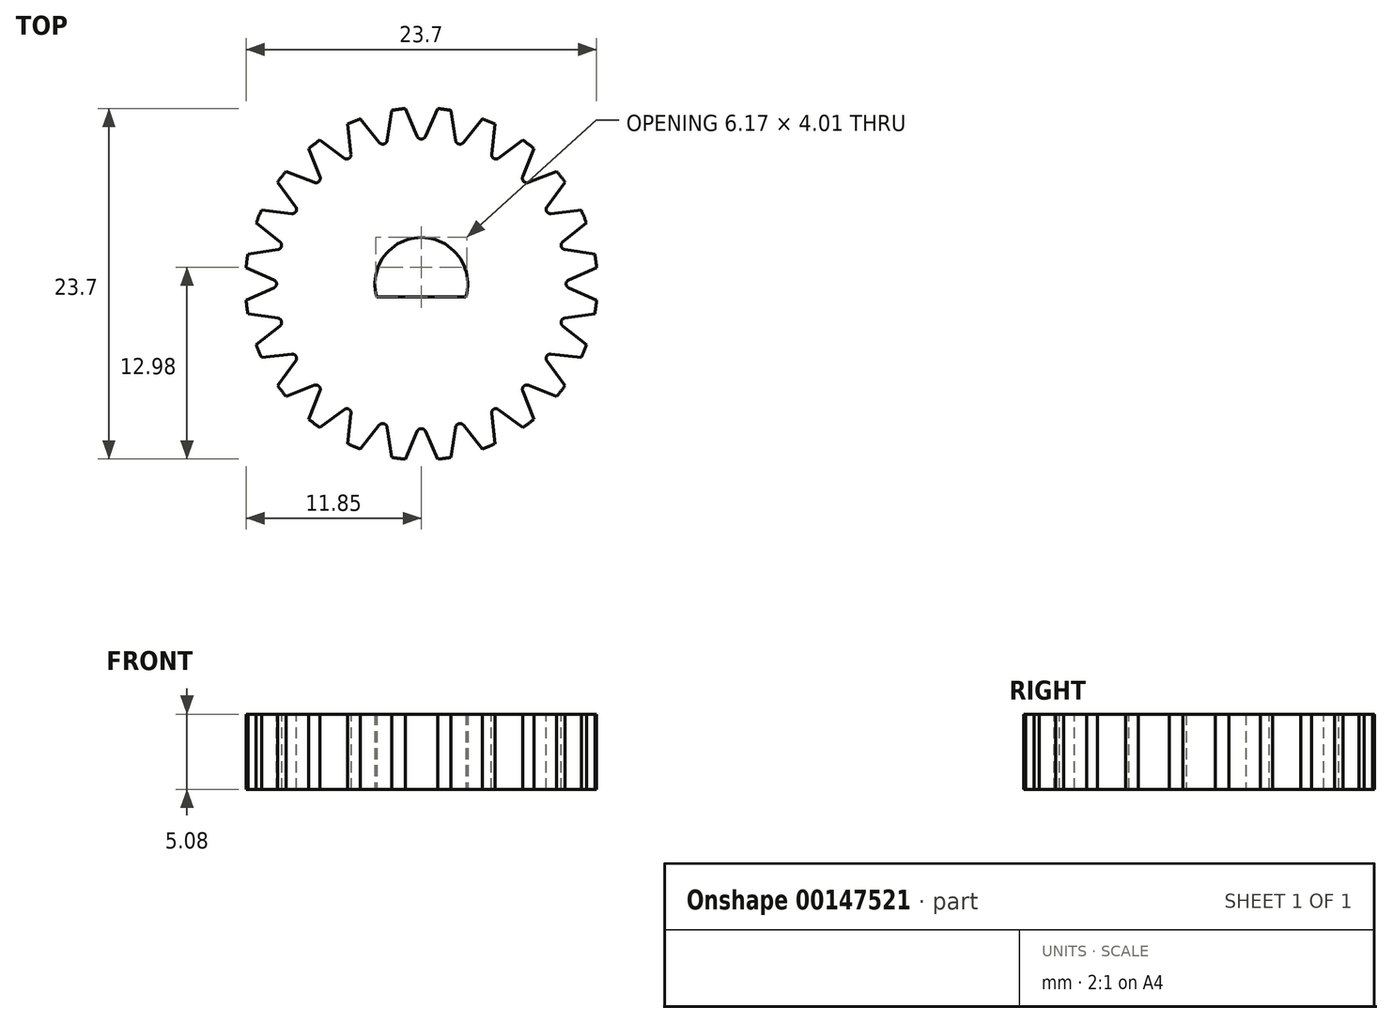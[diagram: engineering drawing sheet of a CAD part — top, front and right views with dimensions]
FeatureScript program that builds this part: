
annotation { "Feature Type Name" : "Feature", "Feature Type Description" : "" }
export const myFeature = defineFeature(function(context is Context, id is Id, definition is map)
    precondition{}
    {
        {
            var Q0;
            Q0=qCreatedBy(makeId("Top.planeOp"),FACE);
            var sketch = newSketch(context, id + "F0", { "sketchPlane" : qUnion([Q0])});
            skCircle(sketch, "E0", {"center": v(0, 0) * mm, "radius": 11.9 * mm});
            skArc(sketch, "E1", {"start": v(3.01, -0.88) * mm, "mid": v(0, 3.14) * mm, "end": v(-3.01, -0.88) * mm});
            skLineSegment(sketch, "E2", {"start": v(0, 0) * mm, "end": v(0, -0.88) * mm, "construction": true});
            skLineSegment(sketch, "E3", {"start": v(-3.01, -0.88) * mm, "end": v(3.01, -0.88) * mm});
            skSolve(sketch);
        }
        {
            var Q0;
            Q0=qSketchRegion(id+"F0",true);
            extrude(context, id + "F1", {"entities" : qUnion([Q0]), "depth" : 5.08 * mm});
        }
        {
            var Q0;
            Q0=makeQuery(id+"F1.opExtrude","CAP_FACE",FACE,{"disambiguationData":[OSD([sQuery(id+"F0.wireOp",EDGE,"E0")])],"isStart":false});
            var sketch = newSketch(context, id + "F2", { "sketchPlane" : qUnion([Q0])});
            skLineSegment(sketch, "E4", {"start": v(0, 0) * mm, "end": v(0, 11.9) * mm});
            skArc(sketch, "E5", {"start": v(1.1, 11.85) * mm, "mid": v(0, 11.9) * mm, "end": v(-1.1, 11.85) * mm});
            skLineSegment(sketch, "E6", {"start": v(-1.1, 11.85) * mm, "end": v(-0.27, 9.97) * mm});
            skLineSegment(sketch, "E7", {"start": v(1.1, 11.85) * mm, "end": v(0.27, 9.97) * mm});
            skArc(sketch, "E8", {"start": v(-0.27, 9.97) * mm, "mid": v(0, 9.79) * mm, "end": v(0.27, 9.97) * mm});
            skLineSegment(sketch, "E9", {"start": v(0, 0) * mm, "end": v(0.74, 11.88) * mm, "construction": true});
            skPoint(sketch, "E10", {"position": v(0.68, 10.9) * mm});
            skSolve(sketch);
        }
        {
            var Q0;
            Q0=qSketchRegion(id+"F2",true);
            var Q1;
            Q1=makeQuery(id+"F1.opExtrude","CAP_FACE",FACE,{"disambiguationData":[OSD([sQuery(id+"F0.wireOp",EDGE,"E0")])],"isStart":true});
            extrude(context, id + "F3", {"entities" : qUnion([Q0]), "operationType" : NewBodyOperationType.REMOVE, "endBound" : BoundingType.UP_TO_SURFACE, "oppositeDirection" : true, "endBoundEntityFace" : qUnion([Q1]), "depth" : 25.4 * mm});
        }
        {
            var Q0;
            Q0=makeQuery(id+"F3.boolean.opBoolean","COPY",FACE,{"derivedFrom":makeQuery(id+"F3.opExtrude","SWEPT_FACE",FACE,{"disambiguationData":[OSD([sQuery(id+"F2.wireOp",EDGE,"E7")])]})});
            var Q1;
            Q1=makeQuery(id+"F3.boolean.opBoolean","COPY",FACE,{"derivedFrom":makeQuery(id+"F3.opExtrude","SWEPT_FACE",FACE,{"disambiguationData":[OSD([sQuery(id+"F2.wireOp",EDGE,"E8")])]})});
            var Q2;
            Q2=makeQuery(id+"F3.boolean.opBoolean","COPY",FACE,{"derivedFrom":makeQuery(id+"F3.opExtrude","SWEPT_FACE",FACE,{"disambiguationData":[OSD([sQuery(id+"F2.wireOp",EDGE,"E6")])]})});
            var Q3;
            Q3=makeQuery(id+"F1.opExtrude","SWEPT_FACE",FACE,{"disambiguationData":[OSD([sQuery(id+"F0.wireOp",EDGE,"E0")])]});
            circularPattern(context, id + "F4", {"patternType" : PatternType.FACE, "faces" : qUnion([Q0, Q1, Q2]), "axis" : qUnion([Q3]), "angle" : 15 * degree, "instanceCount" : 24});
        }
    });
